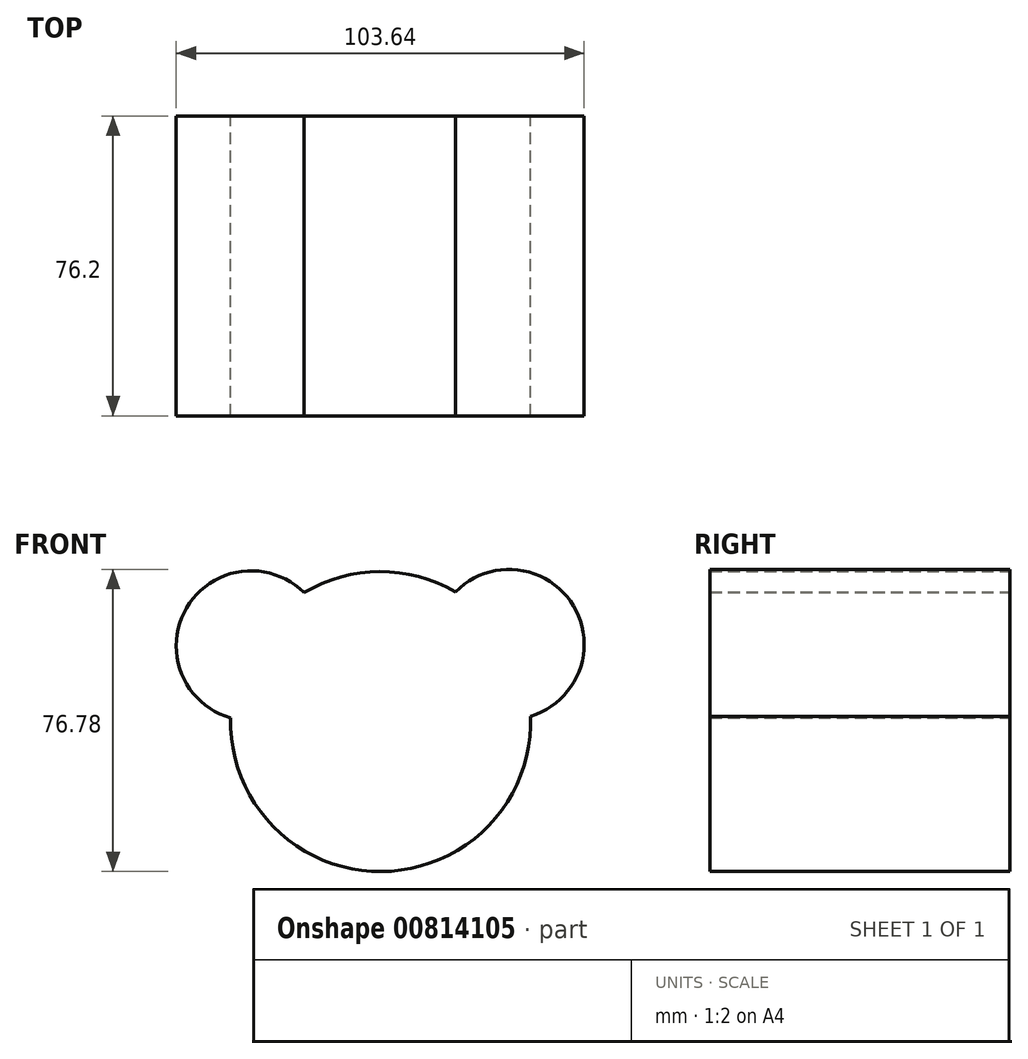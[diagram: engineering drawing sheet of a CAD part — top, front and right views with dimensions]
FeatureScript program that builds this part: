
annotation { "Feature Type Name" : "Feature", "Feature Type Description" : "" }
export const myFeature = defineFeature(function(context is Context, id is Id, definition is map)
    precondition{}
    {
        {
            var Q0;
            Q0=qCreatedBy(makeId("Front.planeOp"),FACE);
            var sketch = newSketch(context, id + "F0", { "sketchPlane" : qUnion([Q0])});
            skCircle(sketch, "E0", {"center": v(0, 0) * mm, "radius": 38.1 * mm});
            skLineSegment(sketch, "E1", {"start": v(0, 0) * mm, "end": v(-32.88, 19.26) * mm});
            skLineSegment(sketch, "E2", {"start": v(0, 0) * mm, "end": v(32.66, 19.63) * mm});
            skCircle(sketch, "E3", {"center": v(-32.88, 19.26) * mm, "radius": 19.05 * mm});
            skCircle(sketch, "E4", {"center": v(32.66, 19.63) * mm, "radius": 19.05 * mm});
            skSolve(sketch);
        }
        {
            var Q0;
            {var subQ3=sQuery(id+"F0.wireOp",EDGE,"E4");var subQ7=sQuery(id+"F0.wireOp",EDGE,"E0");var subQ9=makeQuery(id+"F0.imprint","INTERSECT",VERTEX,{"disambiguationData":[OD(1.0)],"derivedFrom":[subQ7,subQ3]});Q0=makeQuery(id+"F0.imprint","IMPRINT",FACE,{"disambiguationData":[TD([[makeQuery(id+"F0.imprint","IMPRINT",EDGE,{"disambiguationData":[TD([[subQ9,-1.0]])],"derivedFrom":subQ7}),1.0]])]});}
            var Q1;
            {var subQ0=sQuery(id+"F0.wireOp",EDGE,"E0");var subQ1=makeQuery(id+"F0.imprint","INTERSECT",VERTEX,{"derivedFrom":[subQ0,sQuery(id+"F0.wireOp",EDGE,"E2")]});Q1=makeQuery(id+"F0.imprint","IMPRINT",FACE,{"disambiguationData":[TD([[makeQuery(id+"F0.imprint","IMPRINT",EDGE,{"disambiguationData":[TD([[subQ1,1.0]])],"derivedFrom":subQ0}),-1.0]])]});}
            var Q2;
            {var subQ0=sQuery(id+"F0.wireOp",EDGE,"E2");var subQ1=sQuery(id+"F0.wireOp",EDGE,"E0");var subQ2=makeQuery(id+"F0.imprint","INTERSECT",VERTEX,{"derivedFrom":[subQ1,subQ0]});Q2=makeQuery(id+"F0.imprint","IMPRINT",FACE,{"disambiguationData":[TD([[makeQuery(id+"F0.imprint","IMPRINT",EDGE,{"disambiguationData":[TD([[subQ2,1.0]])],"derivedFrom":subQ1}),1.0]])]});}
            var Q3;
            {var subQ0=sQuery(id+"F0.wireOp",EDGE,"E2");var subQ1=sQuery(id+"F0.wireOp",EDGE,"E0");var subQ2=makeQuery(id+"F0.imprint","INTERSECT",VERTEX,{"derivedFrom":[subQ1,subQ0]});Q3=makeQuery(id+"F0.imprint","IMPRINT",FACE,{"disambiguationData":[TD([[makeQuery(id+"F0.imprint","IMPRINT",EDGE,{"disambiguationData":[TD([[subQ2,-1.0]])],"derivedFrom":subQ1}),1.0]])]});}
            var Q4;
            {var subQ3=sQuery(id+"F0.wireOp",EDGE,"E4");var subQ6=sQuery(id+"F0.wireOp",EDGE,"E0");var subQ9=makeQuery(id+"F0.imprint","INTERSECT",VERTEX,{"disambiguationData":[OD(0.0)],"derivedFrom":[subQ6,subQ3]});Q4=makeQuery(id+"F0.imprint","IMPRINT",FACE,{"disambiguationData":[TD([[makeQuery(id+"F0.imprint","IMPRINT",EDGE,{"disambiguationData":[TD([[subQ9,1.0]])],"derivedFrom":subQ6}),1.0]])]});}
            var Q5;
            {var subQ0=sQuery(id+"F0.wireOp",EDGE,"E0");var subQ1=makeQuery(id+"F0.imprint","INTERSECT",VERTEX,{"derivedFrom":[subQ0,sQuery(id+"F0.wireOp",EDGE,"E1")]});Q5=makeQuery(id+"F0.imprint","IMPRINT",FACE,{"disambiguationData":[TD([[makeQuery(id+"F0.imprint","IMPRINT",EDGE,{"disambiguationData":[TD([[subQ1,1.0]])],"derivedFrom":subQ0}),-1.0]])]});}
            var Q6;
            {var subQ0=sQuery(id+"F0.wireOp",EDGE,"E1");var subQ1=sQuery(id+"F0.wireOp",EDGE,"E0");var subQ2=makeQuery(id+"F0.imprint","INTERSECT",VERTEX,{"derivedFrom":[subQ1,subQ0]});Q6=makeQuery(id+"F0.imprint","IMPRINT",FACE,{"disambiguationData":[TD([[makeQuery(id+"F0.imprint","IMPRINT",EDGE,{"disambiguationData":[TD([[subQ2,-1.0]])],"derivedFrom":subQ1}),1.0]])]});}
            var Q7;
            {var subQ0=sQuery(id+"F0.wireOp",EDGE,"E1");var subQ1=sQuery(id+"F0.wireOp",EDGE,"E0");var subQ2=makeQuery(id+"F0.imprint","INTERSECT",VERTEX,{"derivedFrom":[subQ1,subQ0]});Q7=makeQuery(id+"F0.imprint","IMPRINT",FACE,{"disambiguationData":[TD([[makeQuery(id+"F0.imprint","IMPRINT",EDGE,{"disambiguationData":[TD([[subQ2,1.0]])],"derivedFrom":subQ1}),1.0]])]});}
            extrude(context, id + "F1", {"entities" : qUnion([Q0, Q1, Q2, Q3, Q4, Q5, Q6, Q7]), "depth" : 76.2 * mm, "offsetDistance" : 25.4 * mm});
        }
    });
